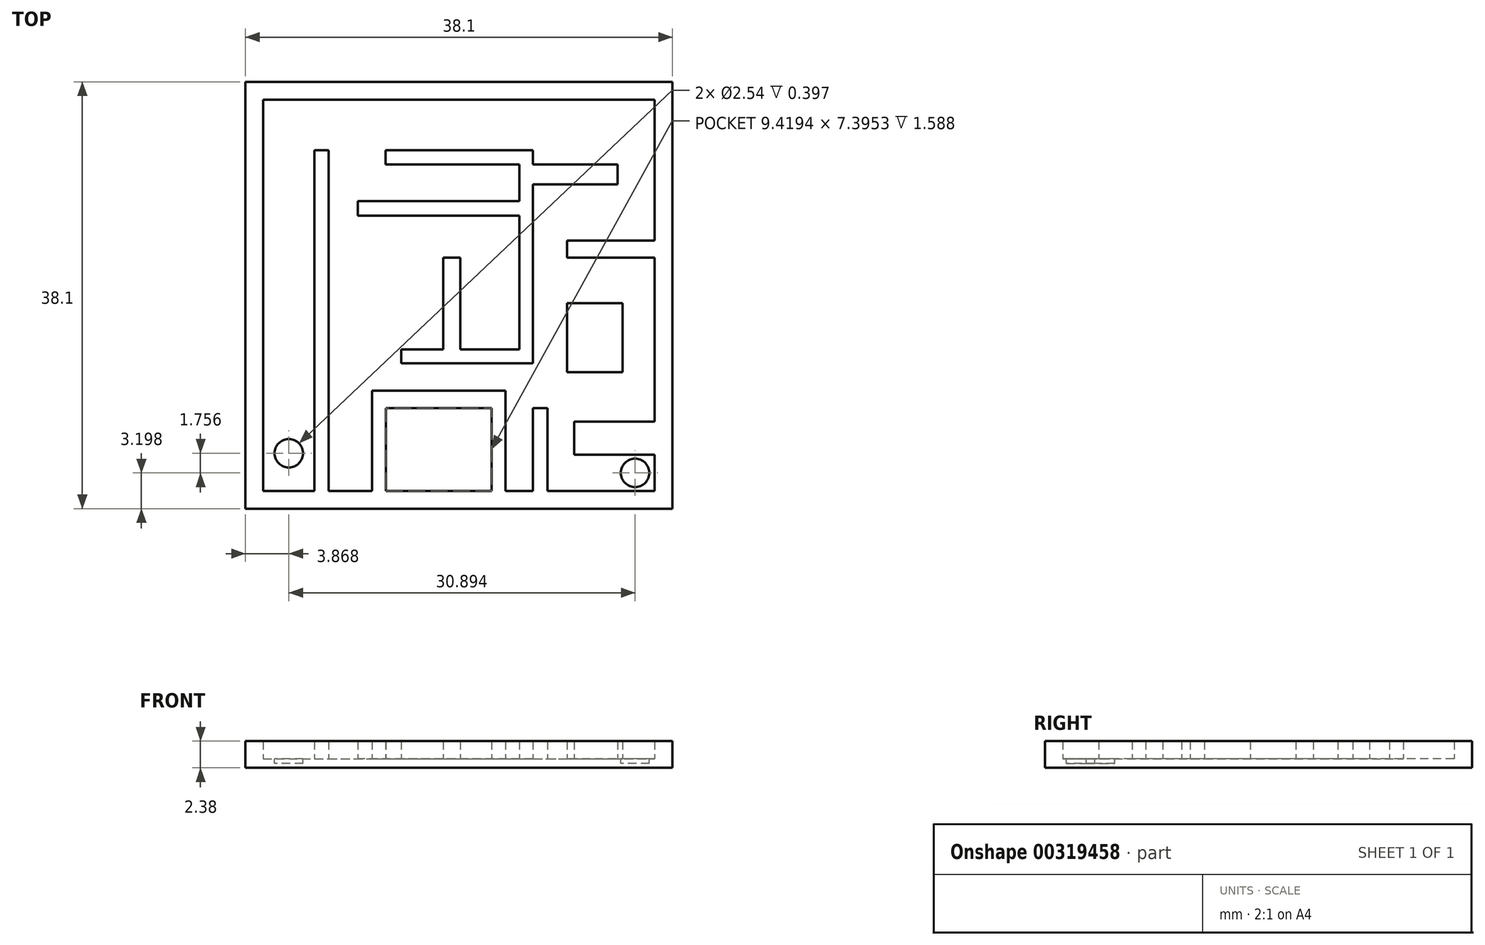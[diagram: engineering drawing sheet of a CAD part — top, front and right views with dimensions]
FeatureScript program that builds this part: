
annotation { "Feature Type Name" : "Feature", "Feature Type Description" : "" }
export const myFeature = defineFeature(function(context is Context, id is Id, definition is map)
    precondition{}
    {
        {
            var Q0;
            Q0=qCreatedBy(makeId("Top.planeOp"),FACE);
            var sketch = newSketch(context, id + "F0", { "sketchPlane" : qUnion([Q0])});
            skLineSegment(sketch, "E0.bottom", {"start": v(-16.1, 12.27) * mm, "end": v(22, 12.27) * mm});
            skLineSegment(sketch, "E0.top", {"start": v(-16.1, -25.83) * mm, "end": v(22, -25.83) * mm});
            skLineSegment(sketch, "E0.left", {"start": v(-16.1, 12.27) * mm, "end": v(-16.1, -25.83) * mm});
            skLineSegment(sketch, "E0.right", {"start": v(22, 12.27) * mm, "end": v(22, -25.83) * mm});
            skSolve(sketch);
        }
        {
            var Q0;
            Q0=makeQuery(id+"F0.imprint","IMPRINT",FACE,{"disambiguationData":[TD([[makeQuery(id+"F0.imprint","IMPRINT",EDGE,{"derivedFrom":sQuery(id+"F0.wireOp",EDGE,"E0.bottom")}),-1.0]])]});
            extrude(context, id + "F1", {"entities" : qUnion([Q0]), "depth" : 0.8 * mm});
        }
        {
            var Q0;
            Q0=makeQuery(id+"F1.opExtrude","CAP_FACE",FACE,{"disambiguationData":[OSD([sQuery(id+"F0.wireOp",EDGE,"E0.bottom"),sQuery(id+"F0.wireOp",EDGE,"E0.top"),sQuery(id+"F0.wireOp",EDGE,"E0.left"),sQuery(id+"F0.wireOp",EDGE,"E0.right")])],"isStart":false});
            var sketch = newSketch(context, id + "F2", { "sketchPlane" : qUnion([Q0])});
            skLineSegment(sketch, "E1.0", {"start": v(-14.51, 10.68) * mm, "end": v(20.41, 10.68) * mm});
            skLineSegment(sketch, "E1.1", {"start": v(-14.51, 10.68) * mm, "end": v(-14.51, -24.24) * mm});
            skLineSegment(sketch, "E1.2", {"start": v(-14.51, -24.24) * mm, "end": v(20.41, -24.24) * mm});
            skLineSegment(sketch, "E1.3", {"start": v(20.41, 10.68) * mm, "end": v(20.41, -24.24) * mm});
            skSolve(sketch);
        }
        {
            var Q0;
            Q0=makeQuery(id+"F2.imprint","IMPRINT",FACE,{"disambiguationData":[TD([[makeQuery(id+"F2.imprint","IMPRINT",EDGE,{"derivedFrom":sQuery(id+"F2.wireOp",EDGE,"E1.0")}),1.0]])]});
            extrude(context, id + "F3", {"entities" : qUnion([Q0]), "operationType" : NewBodyOperationType.ADD, "depth" : 1.59 * mm});
        }
        {
            var Q0;
            Q0=makeQuery(id+"F1.opExtrude","CAP_FACE",FACE,{"disambiguationData":[OSD([sQuery(id+"F0.wireOp",EDGE,"E0.bottom"),sQuery(id+"F0.wireOp",EDGE,"E0.top"),sQuery(id+"F0.wireOp",EDGE,"E0.left"),sQuery(id+"F0.wireOp",EDGE,"E0.right")])],"isStart":false});
            var sketch = newSketch(context, id + "F4", { "sketchPlane" : qUnion([Q0])});
            skLineSegment(sketch, "E2.bottom", {"start": v(-9.95, -24.24) * mm, "end": v(-8.68, -24.24) * mm});
            skLineSegment(sketch, "E2.top", {"start": v(-9.95, 6.16) * mm, "end": v(-8.68, 6.16) * mm});
            skLineSegment(sketch, "E2.left", {"start": v(-9.95, -24.24) * mm, "end": v(-9.95, 6.16) * mm});
            skLineSegment(sketch, "E2.right", {"start": v(-8.68, -24.24) * mm, "end": v(-8.68, 6.16) * mm});
            skLineSegment(sketch, "E3.bottom", {"start": v(-3.6, 6.16) * mm, "end": v(9.54, 6.16) * mm});
            skLineSegment(sketch, "E3.top", {"start": v(-3.6, 4.91) * mm, "end": v(8.35, 4.91) * mm});
            skLineSegment(sketch, "E3.left", {"start": v(-3.6, 6.16) * mm, "end": v(-3.6, 4.91) * mm});
            skLineSegment(sketch, "E3.right", {"start": v(9.54, 6.16) * mm, "end": v(9.54, 4.91) * mm});
            skLineSegment(sketch, "E4.top", {"start": v(9.54, -12.85) * mm, "end": v(8.35, -12.85) * mm});
            skLineSegment(sketch, "E4.left", {"start": v(9.54, 3.12) * mm, "end": v(9.54, -12.85) * mm});
            skLineSegment(sketch, "E4.right", {"start": v(8.35, 4.91) * mm, "end": v(8.35, 1.63) * mm});
            skLineSegment(sketch, "E5.bottom", {"start": v(8.35, -12.85) * mm, "end": v(-2.2, -12.85) * mm});
            skLineSegment(sketch, "E5.top", {"start": v(8.35, -11.6) * mm, "end": v(3.07, -11.6) * mm});
            skLineSegment(sketch, "E5.right", {"start": v(-2.2, -12.85) * mm, "end": v(-2.2, -11.6) * mm});
            skLineSegment(sketch, "E6.bottom", {"start": v(8.35, 1.63) * mm, "end": v(-6.08, 1.63) * mm});
            skLineSegment(sketch, "E6.top", {"start": v(8.35, 0.32) * mm, "end": v(-6.08, 0.32) * mm});
            skLineSegment(sketch, "E6.right", {"start": v(-6.08, 1.63) * mm, "end": v(-6.08, 0.32) * mm});
            skLineSegment(sketch, "E7.bottom", {"start": v(9.54, 4.91) * mm, "end": v(17.11, 4.91) * mm});
            skLineSegment(sketch, "E7.top", {"start": v(9.54, 3.12) * mm, "end": v(17.11, 3.12) * mm});
            skLineSegment(sketch, "E7.right", {"start": v(17.11, 4.91) * mm, "end": v(17.11, 3.12) * mm});
            skPoint(sketch, "E8.oppositeSnap0", {"position": v(3.07, -11.6) * mm});
            skLineSegment(sketch, "E8.top", {"start": v(1.55, -3.43) * mm, "end": v(3.07, -3.43) * mm});
            skLineSegment(sketch, "E8.left", {"start": v(1.55, -11.6) * mm, "end": v(1.55, -3.43) * mm});
            skLineSegment(sketch, "E8.right", {"start": v(3.07, -11.6) * mm, "end": v(3.07, -3.43) * mm});
            skLineSegment(sketch, "E9.bottom", {"start": v(20.41, -1.88) * mm, "end": v(12.58, -1.88) * mm});
            skLineSegment(sketch, "E9.top", {"start": v(20.41, -3.43) * mm, "end": v(12.58, -3.43) * mm});
            skLineSegment(sketch, "E9.left", {"start": v(20.41, -1.88) * mm, "end": v(20.41, -3.43) * mm});
            skLineSegment(sketch, "E9.right", {"start": v(12.58, -1.88) * mm, "end": v(12.58, -3.43) * mm});
            skLineSegment(sketch, "E10.bottom", {"start": v(12.58, -7.49) * mm, "end": v(17.53, -7.49) * mm});
            skLineSegment(sketch, "E10.top", {"start": v(12.58, -13.63) * mm, "end": v(17.53, -13.63) * mm});
            skLineSegment(sketch, "E10.left", {"start": v(12.58, -7.49) * mm, "end": v(12.58, -13.63) * mm});
            skLineSegment(sketch, "E10.right", {"start": v(17.53, -7.49) * mm, "end": v(17.53, -13.63) * mm});
            skLineSegment(sketch, "E11.bottom", {"start": v(-4.83, -24.24) * mm, "end": v(7.1, -24.24) * mm});
            skLineSegment(sketch, "E11.top", {"start": v(-4.83, -15.3) * mm, "end": v(7.1, -15.3) * mm});
            skLineSegment(sketch, "E11.left", {"start": v(-4.83, -24.24) * mm, "end": v(-4.83, -15.3) * mm});
            skLineSegment(sketch, "E11.right", {"start": v(7.1, -24.24) * mm, "end": v(7.1, -15.3) * mm});
            skLineSegment(sketch, "E12.bottom", {"start": v(-3.57, -24.24) * mm, "end": v(5.85, -24.24) * mm});
            skLineSegment(sketch, "E12.top", {"start": v(-3.57, -16.85) * mm, "end": v(5.85, -16.85) * mm});
            skLineSegment(sketch, "E12.left", {"start": v(-3.57, -24.24) * mm, "end": v(-3.57, -16.85) * mm});
            skLineSegment(sketch, "E12.right", {"start": v(5.85, -24.24) * mm, "end": v(5.85, -16.85) * mm});
            skLineSegment(sketch, "E13.bottom", {"start": v(9.54, -24.24) * mm, "end": v(10.85, -24.24) * mm});
            skLineSegment(sketch, "E13.top", {"start": v(9.54, -16.85) * mm, "end": v(10.85, -16.85) * mm});
            skLineSegment(sketch, "E13.left", {"start": v(9.54, -24.24) * mm, "end": v(9.54, -16.85) * mm});
            skLineSegment(sketch, "E13.right", {"start": v(10.85, -24.24) * mm, "end": v(10.85, -16.85) * mm});
            skLineSegment(sketch, "E14.bottom", {"start": v(20.41, -18.04) * mm, "end": v(13.24, -18.04) * mm});
            skLineSegment(sketch, "E14.top", {"start": v(20.41, -21.02) * mm, "end": v(13.24, -21.02) * mm});
            skLineSegment(sketch, "E14.left", {"start": v(20.41, -18.04) * mm, "end": v(20.41, -21.02) * mm});
            skLineSegment(sketch, "E14.right", {"start": v(13.24, -18.04) * mm, "end": v(13.24, -21.02) * mm});
            skLineSegment(sketch, "E15.trimOffspring", {"start": v(1.55, -11.6) * mm, "end": v(-2.2, -11.6) * mm});
            skLineSegment(sketch, "E16.trimOffspring", {"start": v(8.35, 0.32) * mm, "end": v(8.35, -11.6) * mm});
            skSolve(sketch);
        }
        {
            var Q0;
            Q0=makeQuery(id+"F4.imprint","IMPRINT",FACE,{"disambiguationData":[TD([[makeQuery(id+"F4.imprint","IMPRINT",EDGE,{"derivedFrom":sQuery(id+"F4.wireOp",EDGE,"E2.bottom")}),1.0]])]});
            var Q1;
            Q1=makeQuery(id+"F4.imprint","IMPRINT",FACE,{"disambiguationData":[TD([[makeQuery(id+"F4.imprint","IMPRINT",EDGE,{"derivedFrom":sQuery(id+"F4.wireOp",EDGE,"E3.bottom")}),-1.0]])]});
            var Q2;
            Q2=makeQuery(id+"F4.imprint","IMPRINT",FACE,{"disambiguationData":[TD([[makeQuery(id+"F4.imprint","IMPRINT",EDGE,{"derivedFrom":sQuery(id+"F4.wireOp",EDGE,"E9.bottom")}),1.0]])]});
            var Q3;
            Q3=makeQuery(id+"F4.imprint","IMPRINT",FACE,{"disambiguationData":[TD([[makeQuery(id+"F4.imprint","IMPRINT",EDGE,{"derivedFrom":sQuery(id+"F4.wireOp",EDGE,"E10.bottom")}),-1.0]])]});
            var Q4;
            Q4=makeQuery(id+"F4.imprint","IMPRINT",FACE,{"disambiguationData":[TD([[makeQuery(id+"F4.imprint","IMPRINT",EDGE,{"derivedFrom":sQuery(id+"F4.wireOp",EDGE,"E14.bottom")}),1.0]])]});
            var Q5;
            Q5=makeQuery(id+"F4.imprint","IMPRINT",FACE,{"disambiguationData":[TD([[makeQuery(id+"F4.imprint","IMPRINT",EDGE,{"derivedFrom":sQuery(id+"F4.wireOp",EDGE,"E13.bottom")}),1.0]])]});
            var Q6;
            Q6=makeQuery(id+"F4.imprint","IMPRINT",FACE,{"disambiguationData":[TD([[makeQuery(id+"F4.imprint","IMPRINT",EDGE,{"derivedFrom":sQuery(id+"F4.wireOp",EDGE,"E11.top")}),-1.0]])]});
            extrude(context, id + "F5", {"entities" : qUnion([Q0, Q1, Q2, Q3, Q4, Q5, Q6]), "operationType" : NewBodyOperationType.ADD, "depth" : 1.59 * mm});
        }
        {
            var Q0;
            Q0=makeQuery(id+"F5.boolean.opBoolean","SPLIT",FACE,{"disambiguationData":[TD([makeQuery(id+"F3.opExtrude","SWEPT_FACE",FACE,{"disambiguationData":[OSD([sQuery(id+"F2.wireOp",EDGE,"E1.0")])]})])],"derivedFrom":makeQuery(id+"F1.opExtrude","CAP_FACE",FACE,{"disambiguationData":[OSD([sQuery(id+"F0.wireOp",EDGE,"E0.bottom"),sQuery(id+"F0.wireOp",EDGE,"E0.top"),sQuery(id+"F0.wireOp",EDGE,"E0.left"),sQuery(id+"F0.wireOp",EDGE,"E0.right")])],"isStart":false})});
            var sketch = newSketch(context, id + "F6", { "sketchPlane" : qUnion([Q0])});
            skCircle(sketch, "E17", {"center": v(-12.23, -20.88) * mm, "radius": 1.27 * mm});
            skPoint(sketch, "E17.centerSnap0", {"position": v(-12.23, -24.24) * mm});
            skCircle(sketch, "E18", {"center": v(18.66, -22.63) * mm, "radius": 1.27 * mm});
            skPoint(sketch, "E18.centerSnap0", {"position": v(20.41, -22.63) * mm});
            skSolve(sketch);
        }
        {
            var Q0;
            Q0 = qSketchRegion(id + "F6", true);
            extrude(context, id + "F7", {"entities" : qUnion([Q0]), "operationType" : NewBodyOperationType.REMOVE, "oppositeDirection" : true, "depth" : 0.4 * mm});
        }
    });
